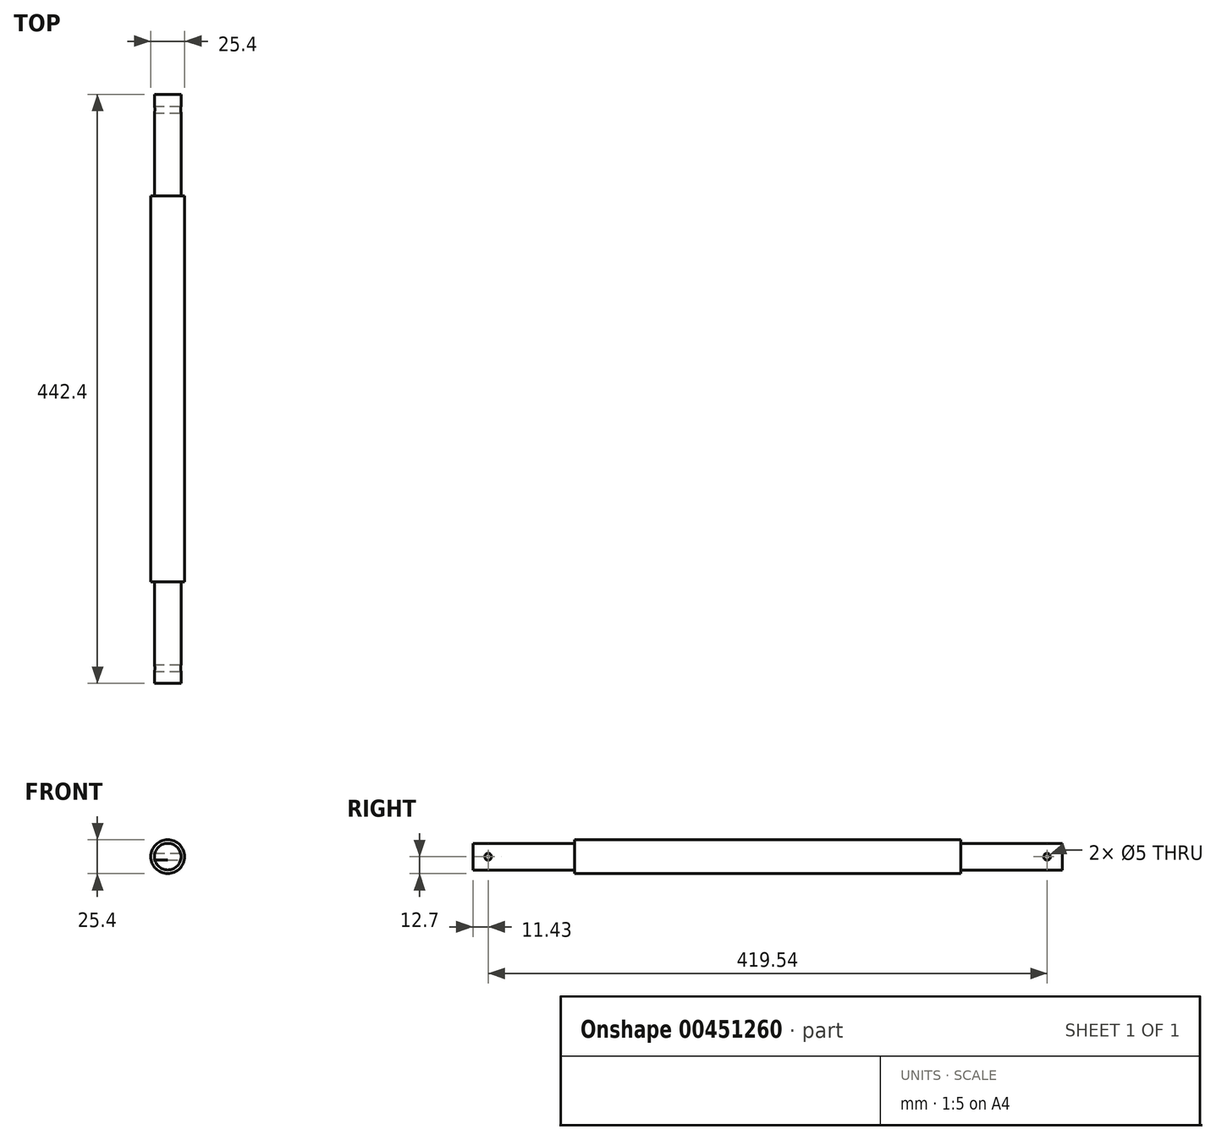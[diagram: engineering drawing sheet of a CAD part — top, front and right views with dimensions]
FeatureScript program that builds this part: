
annotation { "Feature Type Name" : "Feature", "Feature Type Description" : "" }
export const myFeature = defineFeature(function(context is Context, id is Id, definition is map)
    precondition{}
    {
        {
            var Q0;
            Q0=qCreatedBy(makeId("Front.planeOp"),FACE);
            var sketch = newSketch(context, id + "F0", { "sketchPlane" : qUnion([Q0])});
            skCircle(sketch, "E0", {"center": v(0, 0) * mm, "radius": 12.7 * mm});
            skCircle(sketch, "E1", {"center": v(0, 0) * mm, "radius": 10 * mm});
            skSolve(sketch);
        }
        {
            var Q0;
            Q0 = qSketchRegion(id + "F0", true);
            var Q1;
            Q1=makeQuery(id+"F0.imprint","IMPRINT",FACE,{"disambiguationData":[TD([[makeQuery(id+"F0.imprint","IMPRINT",EDGE,{"derivedFrom":sQuery(id+"F0.wireOp",EDGE,"E1")}),1.0]])]});
            extrude(context, id + "F1", {"entities" : qUnion([Q0, Q1]), "oppositeDirection" : true, "depth" : 290 * mm});
        }
        {
            var Q0;
            Q0=makeQuery(id+"F0.imprint","IMPRINT",FACE,{"disambiguationData":[TD([[makeQuery(id+"F0.imprint","IMPRINT",EDGE,{"derivedFrom":sQuery(id+"F0.wireOp",EDGE,"E1")}),1.0]])]});
            extrude(context, id + "F2", {"entities" : qUnion([Q0]), "operationType" : NewBodyOperationType.ADD, "depth" : 76.2 * mm});
        }
        {
            var Q0;
            Q0=makeQuery(id+"F1.opExtrude","CAP_FACE",FACE,{"disambiguationData":[OSD([sQuery(id+"F0.wireOp",EDGE,"E0")])],"isStart":false});
            var sketch = newSketch(context, id + "F3", { "sketchPlane" : qUnion([Q0])});
            skCircle(sketch, "E2", {"center": v(0, 0) * mm, "radius": 10 * mm});
            skSolve(sketch);
        }
        {
            var Q0;
            Q0 = qSketchRegion(id + "F3", true);
            extrude(context, id + "F4", {"entities" : qUnion([Q0]), "operationType" : NewBodyOperationType.ADD, "depth" : 76.2 * mm});
        }
        {
            var Q0;
            Q0=qCreatedBy(makeId("Right.planeOp"),FACE);
            var sketch = newSketch(context, id + "F5", { "sketchPlane" : qUnion([Q0])});
            skCircle(sketch, "E3", {"center": v(-64.77, 0) * mm, "radius": 2.5 * mm});
            skCircle(sketch, "E4", {"center": v(354.77, 0) * mm, "radius": 2.5 * mm});
            skSolve(sketch);
        }
        {
            var Q0;
            Q0 = qSketchRegion(id + "F5", true);
            extrude(context, id + "F6", {"entities" : qUnion([Q0]), "operationType" : NewBodyOperationType.REMOVE, "endBound" : BoundingType.SYMMETRIC, "oppositeDirection" : true, "depth" : 127 * mm});
        }
    });
